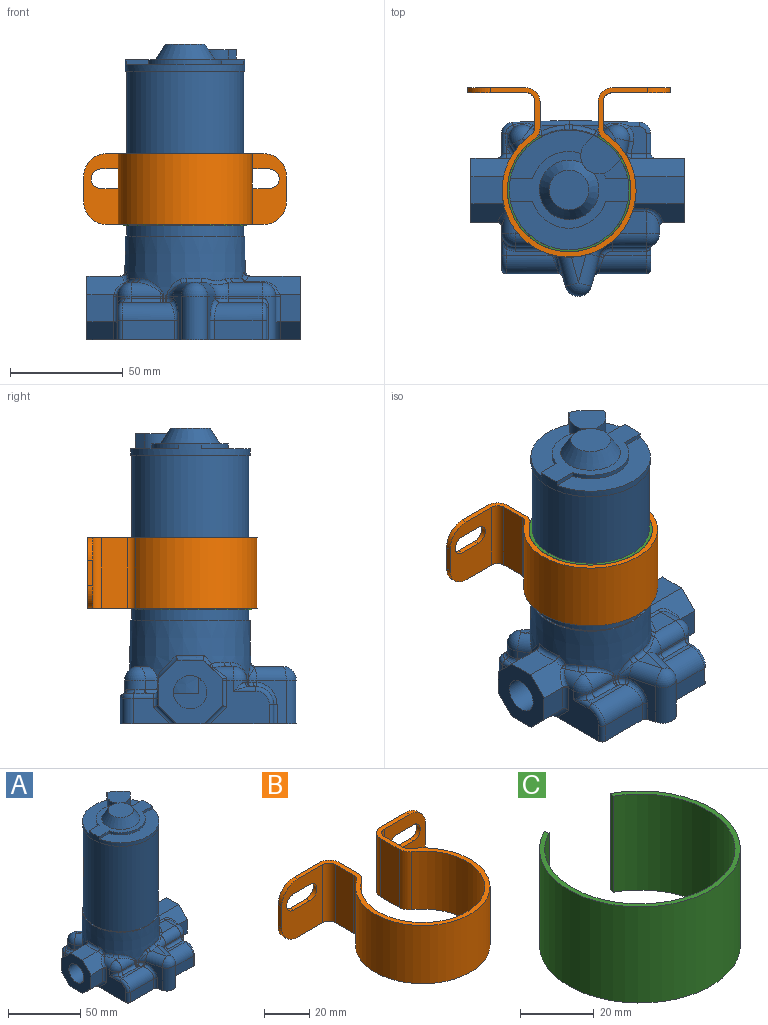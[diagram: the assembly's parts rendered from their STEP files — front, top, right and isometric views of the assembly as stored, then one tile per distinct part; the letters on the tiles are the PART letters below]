
ASSEMBLY  parts=3 mates=2
PART A: 204 faces, bbox 95.3x80.7x150.4 mm
  f0: cylinder r=17mm len=21.52mm, axis (0,0,1), area 54mm2, adj f2,f5,f199,f202
  f1: cylinder r=17mm len=2.33mm, axis (0,0,1), area 5mm2, adj f3,f5,f196,f202
  f2: plane 36.68x21.5mm, normal (0,0,1), area 349.7mm2, adj f0,f40,f199,f201,f202
  f3: plane 10.68x8.71mm, normal (0,0,1), area 52.1mm2, adj f1,f40,f196,f200,f202
  f4: cone r=8.8mm half-angle=32.2deg, axis (0,0,-1), area 571.4mm2, adj f5,f39,f202
  f5: plane 53x34mm, normal (0,0,1), area 511.2mm2, adj f0,f1,f4,f6,f40,f196,f197,f198
  f6: cylinder r=17mm len=32.5mm, axis (0,0,1), area 86.5mm2, adj f5,f7,f197,f198
  f7: plane 52.05x21.5mm, normal (0,0,1), area 553.2mm2, adj f6,f40,f197,f198
  f8: plane 12.8x2.55mm, normal (0,0,1), area 10.9mm2, adj f32,f159,f160
  f9: cone r=26.5mm half-angle=0.9deg, axis (0,0,-1), area 3490.8mm2, adj f37,f48,f97,f98,f99,f100,f101,f114
  f10: plane 11.81x8.92mm, normal (0,-1,0), area 105.1mm2, adj f16,f44,f45,f144,f145
  f11: plane 11.81x11.62mm, normal (0,-1,0), area 136.9mm2, adj f46,f49,f52,f184,f185
  f12: cylinder r=7.41mm len=25mm, axis (-1,0,0), area 790.2mm2, adj f13,f23,f24,f45,f109,f110,f111
  f13: cone r=26.5mm half-angle=0.9deg, axis (0,0,-1), area 77.2mm2, adj f12,f23,f109
  f14: cylinder r=7.41mm len=17.5mm, axis (-1,0,0), area 691.2mm2, adj f15,f18,f52,f53,f112,f113
  f15: cone r=26.5mm half-angle=0.9deg, axis (0,0,-1), area 77.2mm2, adj f14,f18,f113
  f16: plane 8.9x8.1mm, normal (0,-0.71,-0.71), area 101.9mm2, adj f10,f38,f45,f143
  f17: plane 23.55x11.81mm, normal (0,1,0), area 203.3mm2, adj f41,f42,f45,f174,f176,f179,f180,f181
  f18: plane 11.17x3.9mm, normal (0,0,1), area 34.9mm2, adj f14,f15,f53,f113
  f19: plane 12.01x7.35mm, normal (0,0,1), area 69.4mm2, adj f31,f61,f62,f175,f177,f179
  f20: plane 13.25x2.57mm, normal (0,0,1), area 11.5mm2, adj f31,f165,f169
  f21: plane 3.21x1.97mm, normal (0,0,1), area 3.1mm2, adj f64,f152,f153,f154
  f22: plane 14.5x9.1mm, normal (1,0,0), area 124.2mm2, adj f34,f38,f67,f68,f188
  f23: plane 11.17x10.15mm, normal (0,0,1), area 104.7mm2, adj f12,f13,f24,f109
  f24: plane 11.17x6.81mm, normal (1,0,0), area 63.2mm2, adj f12,f23,f109
  f25: cylinder r=8mm len=23.18mm, axis (1,0,0), area 279mm2, adj f27,f29,f66,f139,f141
  f26: cylinder r=8mm len=21.23mm, axis (1,0,0), area 254.5mm2, adj f28,f30,f68,f193,f194
  f27: plane 20.36x3.07mm, normal (0,0,1), area 40.1mm2, adj f25,f33,f133,f134,f135,f138,f142
  f28: plane 18.41x2mm, normal (0,0,1), area 34.8mm2, adj f26,f34,f190,f191,f192
  f29: plane 23.18x8.5mm, normal (0,-1,0), area 197mm2, adj f25,f38,f65,f137
  f30: plane 21.23x8.5mm, normal (0,-1,0), area 180.5mm2, adj f26,f38,f67,f195
  f31: cylinder r=2mm len=31.34mm, axis (-1,0.03,0), area 86.9mm2, adj f19,f20,f32,f55,f62,f162,f171,f173
  f32: cylinder r=2mm len=25.13mm, axis (-1,-0.03,0), area 67.4mm2, adj f8,f31,f56,f63,f157,f158,f161
  f33: cylinder r=2mm len=10mm, axis (0,-1,0), area 20.5mm2, adj f27,f60,f66,f132
  f34: cylinder r=2mm len=3.1mm, axis (0,-1,0), area 8mm2, adj f22,f28,f68,f189
  f35: plane 53x53mm, normal (0,0,-1), area 98.8mm2, adj f36,f40
  f36: cylinder r=25.9mm len=73mm, axis (0,0,1), area 11879.6mm2, adj f35,f37
  f37: plane 53x53mm, normal (0,0,1), area 98.8mm2, adj f9,f36
  f38: plane 95.34x78.84mm, normal (0,0,-1), area 4980.5mm2, adj f16,f22,f29,f30,f41,f45,f49,f51
  f39: plane 17.6x17.6mm, normal (0,0,1), area 243.3mm2, adj f4
  f40: cylinder r=26.5mm len=53mm, axis (0,0,1), area 647mm2, adj f2,f3,f5,f7,f35,f196,f197,f198
  f41: plane 12.85x8.1mm, normal (0,0.71,-0.71), area 147.2mm2, adj f17,f38,f45,f182
  f42: plane 25.42x8.41mm, normal (0,0.71,0.71), area 286.6mm2, adj f17,f43,f45,f114,f115,f172,f174
  f43: plane 22.86x11.81mm, normal (0,0,1), area 265mm2, adj f42,f44,f45,f115
  f44: plane 23.85x8.4mm, normal (0,-0.71,0.71), area 171mm2, adj f10,f43,f45,f115,f116,f145,f146,f147
  f45: plane 28.5x28.25mm, normal (1,0,0), area 497.4mm2, adj f10,f12,f16,f17,f38,f41,f42,f43
  f46: plane 16.56x8.4mm, normal (0,-0.71,0.71), area 169.3mm2, adj f11,f47,f52,f130,f131,f185,f186
  f47: plane 15.36x11.81mm, normal (0,0,1), area 176.4mm2, adj f46,f50,f52,f130
  f48: plane 20.69x13.54mm, normal (0,1,0), area 181.4mm2, adj f9,f50,f51,f52,f128,f150,f151,f152
  f49: plane 11.6x8.1mm, normal (0,-0.71,-0.71), area 132.8mm2, adj f11,f38,f52,f183
  f50: plane 19.22x8.39mm, normal (0,0.71,0.71), area 202.9mm2, adj f47,f48,f52,f128,f130
  f51: plane 11.6x8.1mm, normal (0,0.71,-0.71), area 132.8mm2, adj f38,f48,f52,f149
  f52: plane 28.5x28.25mm, normal (-1,0,0), area 497.4mm2, adj f11,f14,f38,f46,f47,f48,f49,f50
  f53: plane 14.8x12.81mm, normal (-1,0,0), area 95.2mm2, adj f14,f18,f112,f113
  f54: cylinder r=5mm len=11.4mm, axis (0,0,-1), area 88mm2, adj f38,f55,f59,f62
  f55: plane 31.29x11.4mm, normal (0.03,1,0), area 356.8mm2, adj f31,f38,f54,f56
  f56: plane 25.07x11.4mm, normal (-0.03,1,0), area 285.9mm2, adj f32,f38,f55,f57
  f57: cylinder r=5mm len=11.4mm, axis (0,0,-1), area 87.6mm2, adj f38,f56,f58,f63
  f58: plane 16.18x11.4mm, normal (-1,0,0), area 128mm2, adj f38,f57,f64,f149,f150
  f59: plane 16.16x11.4mm, normal (1,0,0), area 127.7mm2, adj f38,f54,f61,f181,f182
  f60: plane 26.02x19.4mm, normal (-1,0,0), area 304mm2, adj f33,f38,f65,f66,f88,f90,f183,f184
  f61: cylinder r=2mm len=8.89mm, axis (0,1,0), area 27.9mm2, adj f19,f59,f62,f180
  f62: torus R=3mm, axis (0,0,-1), area 20.7mm2, adj f19,f31,f54,f61
  f63: torus R=3mm, axis (0,0,-1), area 19.1mm2, adj f32,f57,f64,f156
  f64: cylinder r=2mm len=8.91mm, axis (0,-1,0), area 26.2mm2, adj f21,f58,f63,f151,f155
  f65: cylinder r=2mm len=8.5mm, axis (0,0,-1), area 26.7mm2, adj f29,f38,f60,f66
  f66: torus R=6mm, axis (-1,0,0), area 35.9mm2, adj f25,f33,f60,f65
  f67: cylinder r=2mm len=8.5mm, axis (0,0,-1), area 26.7mm2, adj f22,f30,f38,f68
  f68: torus R=6mm, axis (1,0,0), area 35.9mm2, adj f22,f26,f34,f67
  f69: cylinder r=6mm len=14.66mm, axis (-0.26,0.97,0), area 126.7mm2, adj f70,f71,f83,f86,f121
  f70: sphere r=6mm, area 94.2mm2, adj f69,f72,f80
  f71: torus R=12mm, axis (0,0,1), area 16.5mm2, adj f69,f81,f122
  f72: cylinder r=6mm len=14.66mm, axis (-0.26,-0.97,0), area 127.9mm2, adj f70,f73,f82,f86
  f73: torus R=12mm, axis (0,0,1), area 64mm2, adj f72,f74,f85,f86,f119
  f74: cylinder r=6mm len=14.9mm, axis (-1,0,0), area 138.1mm2, adj f73,f75,f77,f84,f118
  f75: sphere r=6mm, area 56.5mm2, adj f74,f76,f79
  f76: cylinder r=6mm len=9.42mm, axis (0,-1,0), area 62mm2, adj f75,f77,f78,f145,f146
  f77: plane 12.45x9.42mm, normal (0,0,1), area 87.5mm2, adj f74,f76,f117,f147
  f78: plane 19.4x10.02mm, normal (1,0,0), area 79.8mm2, adj f38,f76,f79,f143,f144
  f79: cylinder r=6mm len=19.4mm, axis (0,0,-1), area 126.7mm2, adj f38,f75,f78,f84,f188,f189,f190
  f80: cylinder r=6mm len=19.4mm, axis (0,0,-1), area 304.7mm2, adj f38,f70,f82,f83
  f81: cylinder r=6mm len=3.79mm, axis (0,0,-1), area 4.5mm2, adj f71,f83,f123,f141,f142
  f82: plane 19.4x13.11mm, normal (0.97,-0.26,0), area 112.4mm2, adj f38,f72,f80,f85,f194,f195
  f83: plane 19.4x13.11mm, normal (-0.97,-0.26,0), area 112.4mm2, adj f38,f69,f80,f81,f137,f139
  f84: plane 14.9x0.9mm, normal (0,-1,0), area 13.4mm2, adj f74,f79,f85,f191
  f85: cylinder r=6mm len=5.8mm, axis (0,0,-1), area 7.1mm2, adj f73,f82,f84,f192,f193
  f86: plane 13.23x6.82mm, normal (0,0,1), area 42.3mm2, adj f69,f72,f73,f120
  f87: sphere r=6mm, area 56.5mm2, adj f88,f90,f93
  f88: cylinder r=6mm len=8.81mm, axis (0,1,0), area 54.2mm2, adj f60,f87,f94,f129,f185,f186
  f89: cylinder r=6mm len=1.25mm, axis (0,0,-1), area 1.1mm2, adj f91,f92,f124,f135
  f90: cylinder r=6mm len=6mm, axis (0,0,-1), area 18mm2, adj f60,f87,f91,f132,f133
  f91: plane 12.9x0.9mm, normal (0,-1,0), area 11.6mm2, adj f89,f90,f93,f134
  f92: torus R=12mm, axis (0,0,1), area 1.2mm2, adj f89,f93,f125
  f93: cylinder r=6mm len=12.9mm, axis (-1,0,0), area 79.8mm2, adj f87,f91,f92,f94,f126
  f94: plane 2.92x2.25mm, normal (0,0,1), area 3.1mm2, adj f88,f93,f127
  f95: sphere r=6mm, area 112.4mm2, adj f96,f99,f100
  f96: cylinder r=6mm len=9.69mm, axis (0,0,-1), area 73.3mm2, adj f95,f97,f98,f154,f155,f156,f157
  f97: plane 5.19x4mm, normal (-0.85,-0.53,0), area 24.3mm2, adj f9,f96,f99,f153
  f98: plane 4.82x4.1mm, normal (0.62,0.79,0), area 24.4mm2, adj f9,f96,f100,f158,f159
  f99: cylinder r=6mm len=8.37mm, axis (-0.53,0.85,0), area 48.8mm2, adj f9,f95,f97,f101
  f100: cylinder r=6mm len=8.52mm, axis (0.79,-0.62,0), area 48.8mm2, adj f9,f95,f98,f101
  f101: plane 3.59x3.34mm, normal (0,0,1), area 3.1mm2, adj f9,f99,f100
  f102: sphere r=6mm, area 88.1mm2, adj f103,f106,f107
  f103: cylinder r=6mm len=9.69mm, axis (0,0,-1), area 59.1mm2, adj f102,f104,f105,f173,f175
  f104: plane 4.08x3.84mm, normal (-0.62,0.79,0), area 19.4mm2, adj f103,f107,f164,f169,f171
  f105: plane 5.1x4mm, normal (0.98,-0.21,0), area 20.9mm2, adj f103,f106,f176,f177
  f106: cylinder r=6mm len=9.53mm, axis (-0.21,-0.98,0), area 54.8mm2, adj f102,f105,f108,f168,f172,f174
  f107: cylinder r=6mm len=7.73mm, axis (0.79,0.62,0), area 33.5mm2, adj f102,f104,f108,f163
  f108: plane 2.51x1.76mm, normal (0,0,1), area 1.8mm2, adj f106,f107,f166
  f109: plane 13.45x12.74mm, normal (0,1,0), area 116.1mm2, adj f12,f13,f23,f24,f110,f111
  f110: cylinder r=6mm len=1.29mm, axis (0,-1,0), area 0.6mm2, adj f12,f109,f111
  f111: plane 11.77x3.62mm, normal (1,0,0), area 32mm2, adj f12,f109,f110
  f112: cylinder r=6mm len=1.29mm, axis (0,1,0), area 0.6mm2, adj f14,f53,f113
  f113: plane 6.97x3.25mm, normal (0,1,0), area 22.2mm2, adj f14,f15,f18,f53,f112
  f114: bspline ~8x7.11mm, area 23.7mm2, adj f9,f42,f115,f170
  f115: torus R=28.76mm, axis (0,0,1), area 37.7mm2, adj f9,f42,f43,f44,f114,f116
  f116: bspline ~4.23x3.6mm, area 9.8mm2, adj f9,f44,f115,f148
  f117: torus R=28.8mm, axis (0,0,1), area 32.6mm2, adj f9,f77,f118,f148
  f118: bspline ~5.36x4.34mm, area 8.9mm2, adj f9,f74,f117,f119
  f119: bspline ~13.91x9.06mm, area 30.6mm2, adj f9,f73,f118,f120
  f120: torus R=28.8mm, axis (0,0,1), area 20.5mm2, adj f9,f86,f119,f121
  f121: bspline ~6.31x3.14mm, area 8.2mm2, adj f9,f69,f120,f122
  f122: bspline ~8.42x8.23mm, area 15.7mm2, adj f9,f71,f121,f123
  f123: bspline ~2.37x0.55mm, area 0.3mm2, adj f9,f81,f122,f140
  f124: bspline ~2.37x0.59mm, area 0.3mm2, adj f9,f89,f125,f136
  f125: bspline ~3.44x2.49mm, area 1.2mm2, adj f9,f92,f124,f126
  f126: bspline ~12.62x8.31mm, area 27.5mm2, adj f9,f93,f125,f127
  f127: torus R=28.8mm, axis (0,0,1), area 11mm2, adj f9,f94,f126,f129
  f128: bspline ~10.43x9.37mm, area 31.9mm2, adj f9,f48,f50,f130
  f129: bspline ~9.35x5.24mm, area 16.9mm2, adj f9,f88,f127,f187
  f130: torus R=28.76mm, axis (0,0,1), area 37.7mm2, adj f9,f46,f47,f50,f128,f131
  f131: bspline ~4.84x4.17mm, area 12.1mm2, adj f9,f46,f130,f187
  f132: bspline ~6.93x4mm, area 7.3mm2, adj f33,f90,f133
  f133: torus R=8mm, axis (0,0,-1), area 11.1mm2, adj f27,f90,f132,f134
  f134: cylinder r=2mm len=12.9mm, axis (-1,0,0), area 40.5mm2, adj f27,f91,f133,f135
  f135: torus R=4mm, axis (0,0,-1), area 3.1mm2, adj f27,f89,f134,f136
  f136: sphere r=2mm, area 0.7mm2, adj f124,f135,f138
  f137: cylinder r=2mm len=8.5mm, axis (0,0,1), area 22.3mm2, adj f29,f38,f83,f139
  f138: torus R=28.95mm, axis (0,0,-1), area 3.7mm2, adj f9,f27,f136,f140
  f139: bspline ~9.95x9.07mm, area 37mm2, adj f25,f83,f137,f141
  f140: sphere r=2mm, area 0.7mm2, adj f123,f138,f142
  f141: bspline ~3.8x3.06mm, area 3.9mm2, adj f25,f81,f139,f142
  f142: torus R=4mm, axis (0,0,-1), area 9.1mm2, adj f27,f81,f140,f141
  f143: cylinder r=2mm len=10.1mm, axis (0,0.71,-0.71), area 34.1mm2, adj f16,f38,f78,f144
  f144: cylinder r=2mm len=12.13mm, axis (0,0,-1), area 36.8mm2, adj f10,f78,f143,f145
  f145: torus R=8mm, axis (0,-1,0), area 1.9mm2, adj f10,f44,f76,f144,f146
  f146: bspline ~8.72x8.33mm, area 24.3mm2, adj f44,f76,f145,f147
  f147: cylinder r=2mm len=6.94mm, axis (1,0,0), area 10.9mm2, adj f44,f77,f146,f148
  f148: sphere r=2mm, area 3.7mm2, adj f116,f117,f147
  f149: cylinder r=2mm len=10.1mm, axis (0,-0.71,-0.71), area 34.1mm2, adj f38,f51,f58,f150
  f150: cylinder r=2mm len=4.13mm, axis (0,0,-1), area 11.7mm2, adj f48,f58,f149,f151
  f151: torus R=4mm, axis (0,1,0), area 13.5mm2, adj f48,f64,f150,f152
  f152: cylinder r=2mm len=5.11mm, axis (-1,0,0), area 12.7mm2, adj f9,f21,f48,f151,f153
  f153: cylinder r=2mm len=6.28mm, axis (-0.53,0.85,0), area 15.9mm2, adj f9,f21,f97,f152,f154
  f154: torus R=8mm, axis (0,0,-1), area 2mm2, adj f21,f96,f153,f155
  f155: bspline ~7.23x2.74mm, area 13.8mm2, adj f64,f96,f154,f156
  f156: bspline ~5.22x5.14mm, area 12.9mm2, adj f63,f96,f155,f157
  f157: bspline ~10.49x2.6mm, area 16.6mm2, adj f32,f96,f156,f158
  f158: bspline ~3.55x2.8mm, area 3.5mm2, adj f32,f98,f157,f159
  f159: cylinder r=2mm len=4.93mm, axis (0.79,-0.62,0), area 13.3mm2, adj f8,f9,f98,f158,f160
  f160: torus R=29mm, axis (0,0,-1), area 33mm2, adj f8,f9,f159,f161
  f161: bspline ~4.78x2.27mm, area 5.8mm2, adj f9,f32,f160,f162
  f162: bspline ~3.61x2.07mm, area 4.7mm2, adj f9,f31,f161,f165
  f163: bspline ~9.67x8.86mm, area 28mm2, adj f9,f107,f164,f166
  f164: bspline ~75.94x3.14mm, area 8.7mm2, adj f9,f104,f163,f167
  f165: torus R=29mm, axis (0,0,-1), area 32.1mm2, adj f9,f20,f162,f167
  f166: torus R=28.8mm, axis (0,0,1), area 4.9mm2, adj f9,f108,f163,f168
  f167: sphere r=2mm, area 2.2mm2, adj f164,f165,f169
  f168: bspline ~10.18x6.85mm, area 21.2mm2, adj f9,f106,f166,f170
  f169: cylinder r=2mm len=4.05mm, axis (0.79,0.62,0), area 11.2mm2, adj f20,f104,f167,f171
  f170: sphere r=2mm, area 2mm2, adj f114,f168,f172
  f171: bspline ~2.2x2.04mm, area 3.2mm2, adj f31,f104,f169,f173
  f172: bspline ~4.73x3.41mm, area 10.4mm2, adj f42,f106,f170,f174
  f173: bspline ~11.52x2.93mm, area 21.9mm2, adj f31,f103,f171,f175
  f174: bspline ~2.42x2.07mm, area 2mm2, adj f17,f42,f106,f172,f176
  f175: torus R=8mm, axis (0,0,-1), area 19.5mm2, adj f19,f103,f173,f177
  f176: cylinder r=2mm len=4mm, axis (0,0,1), area 14.3mm2, adj f17,f105,f174,f178
  f177: cylinder r=2mm len=5.52mm, axis (-0.21,-0.98,0), area 16.4mm2, adj f19,f105,f175,f178
  f178: sphere r=2mm, area 7.1mm2, adj f176,f177,f179
  f179: cylinder r=2mm len=6.69mm, axis (-1,0,0), area 21mm2, adj f17,f19,f178,f180
  f180: torus R=4mm, axis (0,1,0), area 13.5mm2, adj f17,f61,f179,f181
  f181: cylinder r=2mm len=4.13mm, axis (0,0,1), area 11.7mm2, adj f17,f59,f180,f182
  f182: cylinder r=2mm len=10.1mm, axis (0,0.71,0.71), area 34.1mm2, adj f38,f41,f59,f181
  f183: cylinder r=2mm len=10.1mm, axis (0,-0.71,0.71), area 34.1mm2, adj f38,f49,f60,f184
  f184: cylinder r=2mm len=12.13mm, axis (0,0,1), area 36.8mm2, adj f11,f60,f183,f185
  f185: torus R=8mm, axis (0,-1,0), area 1.9mm2, adj f11,f46,f88,f184,f186
  f186: bspline ~8.53x7.2mm, area 19.7mm2, adj f46,f88,f185,f187
  f187: sphere r=2mm, area 3mm2, adj f129,f131,f186
  f188: cylinder r=2mm len=14.5mm, axis (0,0,-1), area 30.2mm2, adj f22,f38,f79,f189
  f189: bspline ~4.83x3.63mm, area 10.5mm2, adj f34,f79,f188,f190
  f190: torus R=8mm, axis (0,0,-1), area 0.1mm2, adj f28,f79,f189,f191
  f191: cylinder r=2mm len=14.9mm, axis (-1,0,0), area 46.8mm2, adj f28,f84,f190,f192
  f192: torus R=4mm, axis (0,0,-1), area 17.3mm2, adj f28,f85,f191,f193
  f193: bspline ~3.8x3.06mm, area 3.9mm2, adj f26,f85,f192,f194
  f194: bspline ~9.95x9.07mm, area 37mm2, adj f26,f82,f193,f195
  f195: cylinder r=2mm len=8.5mm, axis (0,0,-1), area 22.3mm2, adj f30,f38,f82,f194
  f196: plane 9.78x2mm, normal (0,1,0), area 19.6mm2, adj f1,f3,f5,f40
  f197: plane 9.78x2mm, normal (0,-1,0), area 19.6mm2, adj f5,f6,f7,f40
  f198: plane 9.78x2mm, normal (0,-1,0), area 19.6mm2, adj f5,f6,f7,f40
  f199: plane 9.78x2mm, normal (0,1,0), area 19.6mm2, adj f0,f2,f5,f40
  f200: plane 6.6x3.96mm, normal (0.75,-0.66,0), area 34.7mm2, adj f3,f40,f202,f203
  f201: plane 6.6x3.96mm, normal (-0.75,0.66,0), area 34.7mm2, adj f2,f40,f202,f203
  f202: cylinder r=8mm len=14.01mm, axis (0,0,-1), area 125.3mm2, adj f0,f1,f2,f3,f4,f5,f200,f201
  f203: plane 17.48x17.23mm, normal (0,0,1), area 198mm2, adj f40,f200,f201,f202
PART B: 34 faces, bbox 89.8x75.1x31.4 mm
  f0: plane 31.4x25.75mm, normal (0,1,0), area 618.2mm2, adj f7,f8,f20,f21,f22,f23,f30,f31
  f1: plane 31.4x25.75mm, normal (0,-1,0), area 618.2mm2, adj f8,f9,f20,f21,f22,f23,f30,f31
  f2: plane 31.4x25.75mm, normal (0,-1,0), area 618.2mm2, adj f15,f16,f20,f21,f24,f25,f26,f27
  f3: plane 31.4x25.75mm, normal (0,1,0), area 618.2mm2, adj f16,f17,f20,f21,f24,f25,f26,f27
  f4: cylinder r=27.35mm len=54.7mm, axis (0,0,-1), area 4354.3mm2, adj f5,f19,f20,f21
  f5: cylinder r=6.25mm len=31.4mm, axis (0,0,-1), area 189.3mm2, adj f4,f6,f20,f21
  f6: plane 31.4x11.54mm, normal (1,0,0), area 362.4mm2, adj f5,f7,f20,f21
  f7: cylinder r=6.25mm len=31.4mm, axis (0,0,-1), area 308.3mm2, adj f0,f6,f20,f21
  f8: plane 11.4x2.25mm, normal (-1,0,0), area 25.7mm2, adj f0,f1,f22,f23
  f9: cylinder r=4mm len=31.4mm, axis (0,0,-1), area 197.3mm2, adj f1,f10,f20,f21
  f10: plane 31.4x11.42mm, normal (-1,0,0), area 358.6mm2, adj f9,f11,f20,f21
  f11: cylinder r=4mm len=31.4mm, axis (0,0,-1), area 121.4mm2, adj f10,f12,f20,f21
  f12: cylinder r=29.7mm len=59.4mm, axis (0,0,-1), area 4732.3mm2, adj f11,f13,f20,f21
  f13: cylinder r=4mm len=31.4mm, axis (0,0,-1), area 121.4mm2, adj f12,f14,f20,f21
  f14: plane 31.4x11.42mm, normal (1,0,0), area 358.6mm2, adj f13,f15,f20,f21
  f15: cylinder r=4mm len=31.4mm, axis (0,0,-1), area 197.3mm2, adj f2,f14,f20,f21
  f16: plane 11.4x2.25mm, normal (1,0,0), area 25.7mm2, adj f2,f3,f24,f25
  f17: cylinder r=6.25mm len=31.4mm, axis (0,0,-1), area 308.3mm2, adj f3,f18,f20,f21
  f18: plane 31.4x11.54mm, normal (-1,0,0), area 362.4mm2, adj f17,f19,f20,f21
  f19: cylinder r=6.25mm len=31.4mm, axis (0,0,-1), area 189.3mm2, adj f4,f18,f20,f21
  f20: plane 75.1x69.8mm, normal (0,0,1), area 521.6mm2, adj f0,f1,f2,f3,f4,f5,f6,f7
  f21: plane 75.1x69.8mm, normal (0,0,-1), area 521.6mm2, adj f0,f1,f2,f3,f4,f5,f6,f7
  f22: cylinder r=10mm len=10mm, axis (0,1,0), area 35.3mm2, adj f0,f1,f8,f21
  f23: cylinder r=10mm len=10mm, axis (0,-1,0), area 35.3mm2, adj f0,f1,f8,f20
  f24: cylinder r=10mm len=10mm, axis (0,-1,0), area 35.3mm2, adj f2,f3,f16,f21
  f25: cylinder r=10mm len=10mm, axis (0,1,0), area 35.3mm2, adj f2,f3,f16,f20
  f26: cylinder r=4.36mm len=8.71mm, axis (0,-1,0), area 30.8mm2, adj f2,f3,f27,f29
  f27: plane 10.09x2.25mm, normal (0,0,1), area 22.7mm2, adj f2,f3,f26,f28
  f28: cylinder r=4.36mm len=8.71mm, axis (0,-1,0), area 30.8mm2, adj f2,f3,f27,f29
  f29: plane 10.09x2.25mm, normal (0,0,-1), area 22.7mm2, adj f2,f3,f26,f28
  f30: cylinder r=4.36mm len=8.71mm, axis (0,-1,0), area 30.8mm2, adj f0,f1,f31,f33
  f31: plane 10.09x2.25mm, normal (0,0,1), area 22.7mm2, adj f0,f1,f30,f32
  f32: cylinder r=4.36mm len=8.71mm, axis (0,-1,0), area 30.8mm2, adj f0,f1,f31,f33
  f33: plane 10.09x2.25mm, normal (0,0,-1), area 22.7mm2, adj f0,f1,f30,f32
PART C: 6 faces, bbox 54.7x51.6x32 mm
  f0: cylinder r=25.9mm len=51.8mm, axis (0,0,-1), area 4387.9mm2, adj f1,f3,f4,f5
  f1: plane 32x1.48mm, normal (-0.98,0.21,0), area 48.3mm2, adj f0,f2,f4,f5
  f2: cylinder r=27.35mm len=54.7mm, axis (0,0,-1), area 4653.2mm2, adj f1,f3,f4,f5
  f3: plane 32x1.37mm, normal (0.94,0.35,0), area 46.7mm2, adj f0,f2,f4,f5
  f4: plane 54.7x51.64mm, normal (0,0,1), area 204.8mm2, adj f0,f1,f2,f3
  f5: plane 54.7x51.64mm, normal (0,0,-1), area 204.8mm2, adj f0,f1,f2,f3
PLACE A t=(102.71,22.06,-92.36)mm
PLACE B t=(102.71,22.06,-39.56)mm
PLACE C t=(102.71,22.06,-39.86)mm
MATE fastened A.f4 <-> B.f4  axis (0,0,1) through (102.71,22.06,-23.86)mm
MATE fastened A.f4 <-> C.f0  axis (0,0,1) through (102.71,22.06,-23.86)mm
